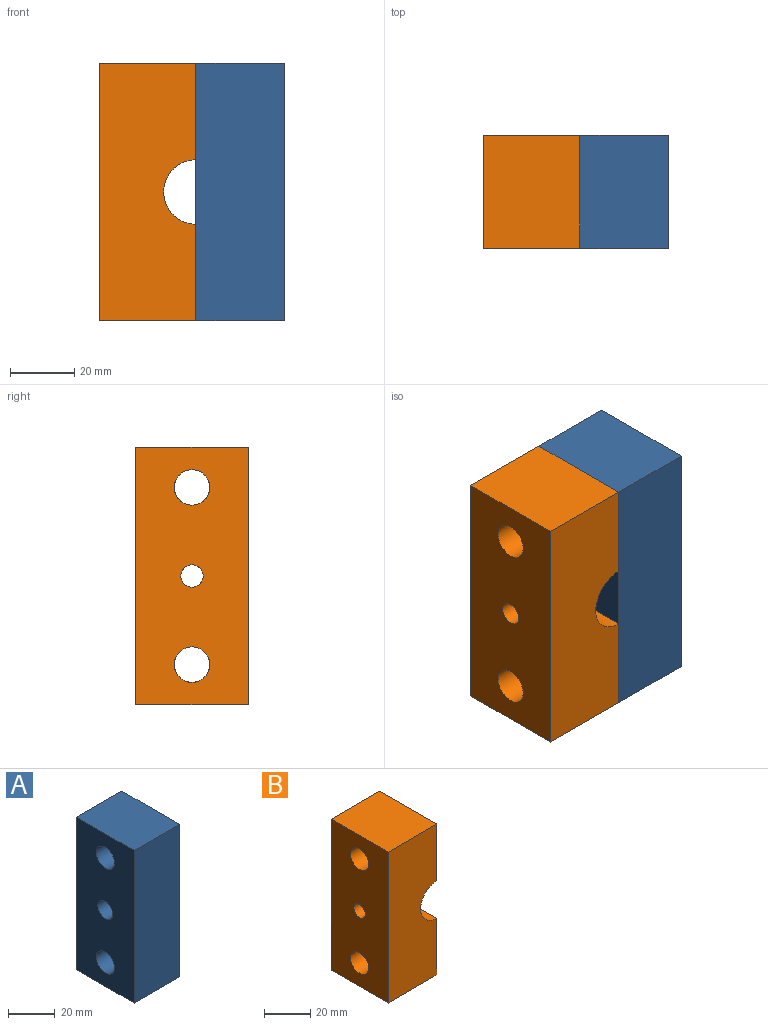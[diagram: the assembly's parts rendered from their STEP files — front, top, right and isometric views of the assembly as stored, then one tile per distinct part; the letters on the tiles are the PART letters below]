
ASSEMBLY  parts=2 mates=1
PART A: 13 faces, bbox 27.5x35x80 mm
  f0: plane 35x27.5mm, normal (0,0,-1), area 962.5mm2, adj f1,f3,f4,f5
  f1: plane 80x35mm, normal (1,0,0), area 2269mm2, adj f0,f2,f4,f5,f6,f9,f12
  f2: plane 35x27.5mm, normal (0,0,1), area 962.5mm2, adj f1,f3,f4,f5
  f3: plane 80x35mm, normal (-1,0,0), area 2546.3mm2, adj f0,f2,f4,f5,f6,f7,f10
  f4: plane 80x27.5mm, normal (0,-1,0), area 2200mm2, adj f0,f1,f2,f3
  f5: plane 80x27.5mm, normal (0,1,0), area 2200mm2, adj f0,f1,f2,f3
  f6: cylinder r=4.5mm len=27.5mm, axis (1,0,0), area 777.5mm2, adj f1,f3
  f7: cylinder r=5.5mm len=17.5mm, axis (1,0,0), area 604.8mm2, adj f3,f8
  f8: plane 17.25x17.25mm, normal (1,0,0), area 138.7mm2, adj f7,f9
  f9: cylinder r=8.62mm len=17.25mm, axis (1,0,0), area 541.9mm2, adj f1,f8
  f10: cylinder r=5.5mm len=17.5mm, axis (1,0,0), area 604.8mm2, adj f3,f11
  f11: plane 17.25x17.25mm, normal (1,0,0), area 138.7mm2, adj f10,f12
  f12: cylinder r=8.62mm len=17.25mm, axis (1,0,0), area 541.9mm2, adj f1,f11
PART B: 11 faces, bbox 29.9x35x80 mm
  f0: cylinder r=10mm len=35mm, axis (0,1,0), area 1060.4mm2, adj f3,f4,f6,f7,f10
  f1: plane 80x35mm, normal (-1,0,0), area 2571.4mm2, adj f2,f5,f6,f7,f8,f9,f10
  f2: plane 35x29.9mm, normal (0,0,-1), area 1046.5mm2, adj f1,f3,f6,f7
  f3: plane 35x30mm, normal (1,0,0), area 955mm2, adj f0,f2,f6,f7,f9
  f4: plane 35x30mm, normal (1,0,0), area 955mm2, adj f0,f5,f6,f7,f8
  f5: plane 35x29.9mm, normal (0,0,1), area 1046.5mm2, adj f1,f4,f6,f7
  f6: plane 80x29.9mm, normal (0,-1,0), area 2234.9mm2, adj f0,f1,f2,f3,f4,f5
  f7: plane 80x29.9mm, normal (0,1,0), area 2234.9mm2, adj f0,f1,f2,f3,f4,f5
  f8: cylinder r=5.5mm len=29.9mm, axis (1,0,0), area 1033.3mm2, adj f1,f4
  f9: cylinder r=5.5mm len=29.9mm, axis (1,0,0), area 1033.3mm2, adj f1,f3
  f10: cylinder r=3.5mm len=20.53mm, axis (1,0,0), area 444.5mm2, adj f0,f1
PLACE A t=(-28.61,8.85,-7.87)mm
PLACE B t=(-22.62,8.85,-7.87)mm
MATE fastened A.f7 <-> B.f8  axis (-1,0,0) through (-7.67,-8.65,19.63)mm
